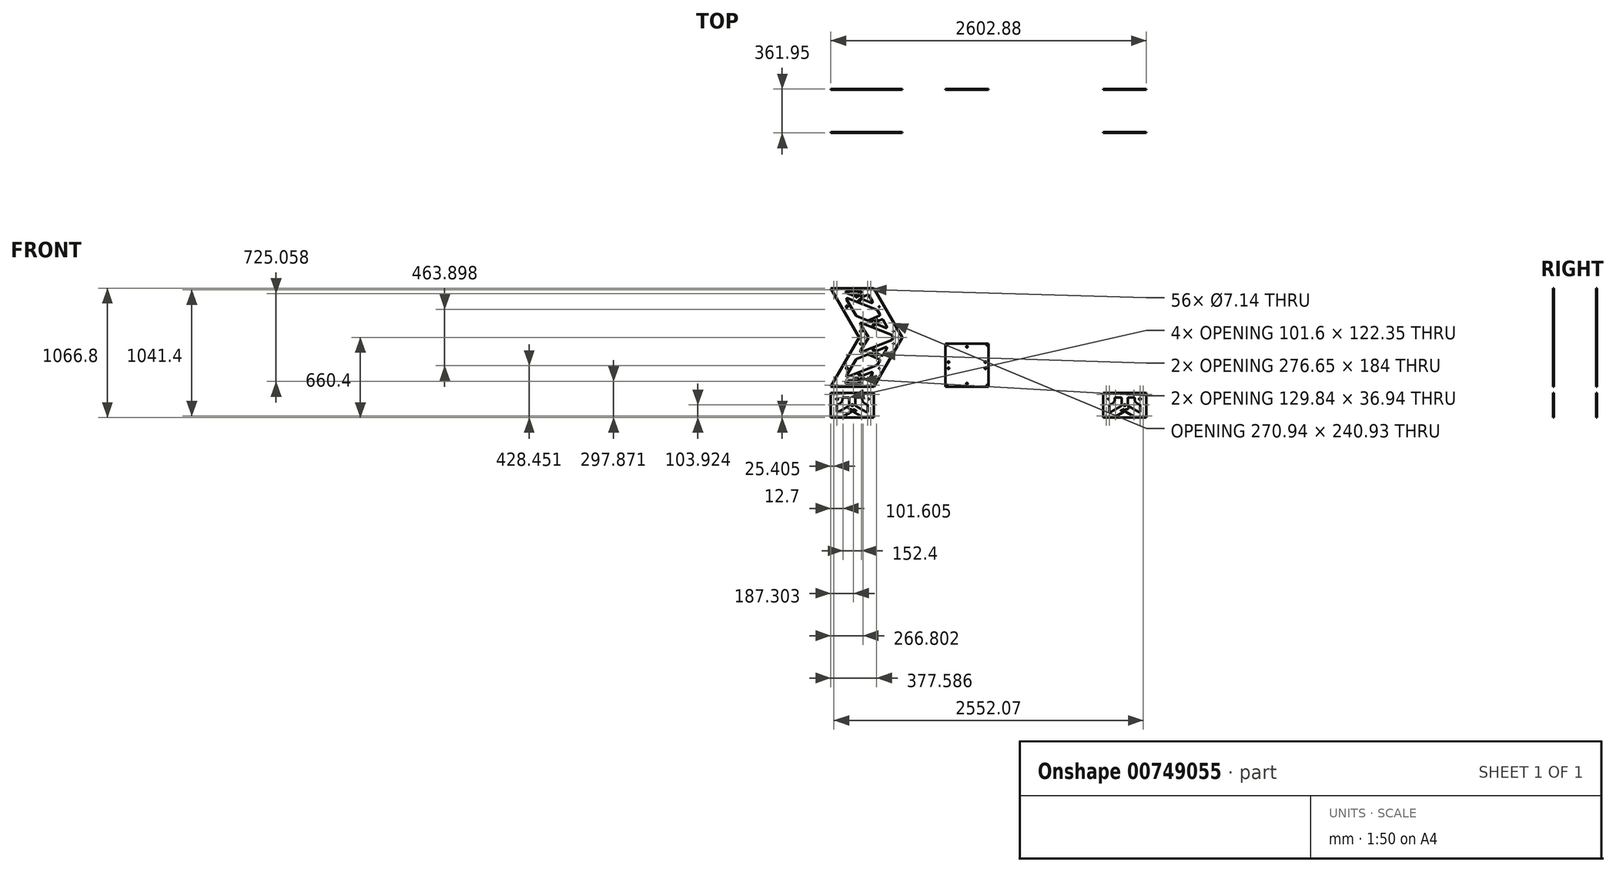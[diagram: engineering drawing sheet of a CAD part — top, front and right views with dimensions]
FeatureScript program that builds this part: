
annotation { "Feature Type Name" : "Feature", "Feature Type Description" : "" }
export const myFeature = defineFeature(function(context is Context, id is Id, definition is map)
    precondition{}
    {
        {
            var Q0;
            Q0=qCreatedBy(makeId("Front.planeOp"),FACE);
            var sketch = newSketch(context, id + "F0", { "sketchPlane" : qUnion([Q0])});
            skLineSegment(sketch, "E0.bottom", {"start": v(0, 0) * mm, "end": v(355.6, 0) * mm});
            skLineSegment(sketch, "E0.top", {"start": v(0, 355.6) * mm, "end": v(355.6, 355.6) * mm});
            skLineSegment(sketch, "E0.left", {"start": v(0, 0) * mm, "end": v(0, 355.6) * mm});
            skLineSegment(sketch, "E0.right", {"start": v(355.6, 0) * mm, "end": v(355.6, 355.6) * mm});
            skLineSegment(sketch, "E1", {"start": v(177.8, 355.6) * mm, "end": v(177.8, 0) * mm, "construction": true});
            skLineSegment(sketch, "E2", {"start": v(355.6, 177.8) * mm, "end": v(0, 177.8) * mm, "construction": true});
            skPoint(sketch, "E3", {"position": v(12.7, 342.9) * mm});
            skPoint(sketch, "E4.MirrorP", {"position": v(342.9, 342.9) * mm});
            skPoint(sketch, "E5.MirrorP", {"position": v(342.9, 12.7) * mm});
            skPoint(sketch, "E6.MirrorP", {"position": v(12.7, 12.7) * mm});
            skSolve(sketch);
        }
        {
            var Q0;
            Q0 = qSketchRegion(id + "F0", true);
            extrude(context, id + "F1", {"entities" : qUnion([Q0]), "depth" : 6.35 * mm, "offsetDistance" : 25.4 * mm});
        }
        {
            var Q0;
            Q0=sQuery(id+"F0.wireOp",VERTEX,"E3");
            var Q1;
            Q1=sQuery(id+"F0.wireOp",VERTEX,"E4.MirrorP");
            var Q2;
            Q2=sQuery(id+"F0.wireOp",VERTEX,"E5.MirrorP");
            var Q3;
            Q3=sQuery(id+"F0.wireOp",VERTEX,"E6.MirrorP");
            var Q4;
            Q4=makeQuery(id+"F1.opExtrude","SWEPT_BODY",BODY,{"disambiguationData":[OSD([sQuery(id+"F0.wireOp",EDGE,"E0.bottom"),sQuery(id+"F0.wireOp",EDGE,"E0.top"),sQuery(id+"F0.wireOp",EDGE,"E0.left"),sQuery(id+"F0.wireOp",EDGE,"E0.right")])]});
            hole(context, id + "F2", {"style" : HoleStyle.SIMPLE, "endStyle" : HoleEndStyle.BLIND, "oppositeDirection" : true, "standardTappedOrClearance" : lookupTablePath({ "standard" : "ANSI", "fit" : "Normal (ASME)", "size" : "1/4", "type" : "Clearance" }), "standardBlindInLast" : lookupTablePath({ "fit" : "Free", "standard" : "ANSI", "size" : "1/4", "type" : "Clearance" }), "holeDiameter" : 6.76 * mm, "majorDiameter" : 6.35 * mm, "holeDepth" : 26.06 * mm, "isTappedThrough" : true, "tappedDepth" : 22.25 * mm, "tapClearance" : 3, "locations" : qUnion([Q0, Q1, Q2, Q3]), "scope" : qUnion([Q4])});
        }
        {
            var Q0;
            Q0=makeQuery(id+"F1.opExtrude","CAP_FACE",FACE,{"disambiguationData":[OSD([sQuery(id+"F0.wireOp",EDGE,"E0.bottom"),sQuery(id+"F0.wireOp",EDGE,"E0.top"),sQuery(id+"F0.wireOp",EDGE,"E0.left"),sQuery(id+"F0.wireOp",EDGE,"E0.right")])],"isStart":false});
            var sketch = newSketch(context, id + "F3", { "sketchPlane" : qUnion([Q0])});
            skLineSegment(sketch, "E7", {"start": v(177.8, 355.6) * mm, "end": v(177.8, 0) * mm, "construction": true});
            skLineSegment(sketch, "E8", {"start": v(0, 177.8) * mm, "end": v(355.6, 177.8) * mm, "construction": true});
            skCircle(sketch, "E9", {"center": v(25.4, 203.2) * mm, "radius": 6.35 * mm});
            skCircle(sketch, "E10", {"center": v(177.8, 330.2) * mm, "radius": 6.35 * mm});
            skCircle(sketch, "E11.MirrorC", {"center": v(330.2, 203.2) * mm, "radius": 6.35 * mm});
            skCircle(sketch, "E12.MirrorC", {"center": v(25.4, 152.4) * mm, "radius": 6.35 * mm});
            skCircle(sketch, "E13.MirrorC", {"center": v(330.2, 152.4) * mm, "radius": 6.35 * mm});
            skCircle(sketch, "E14.MirrorC", {"center": v(177.8, 25.4) * mm, "radius": 6.35 * mm});
            skSolve(sketch);
        }
        {
            var Q0;
            Q0 = qSketchRegion(id + "F3", true);
            extrude(context, id + "F4", {"entities" : qUnion([Q0]), "operationType" : NewBodyOperationType.REMOVE, "oppositeDirection" : true, "depth" : 25.4 * mm, "offsetDistance" : 25.4 * mm});
        }
        {
            var Q0;
            Q0=qCreatedBy(makeId("Front.planeOp"),FACE);
            var sketch = newSketch(context, id + "F5", { "sketchPlane" : qUnion([Q0])});
            skLineSegment(sketch, "E15", {"start": v(-590.24, 0) * mm, "end": v(-945.84, 0) * mm});
            skLineSegment(sketch, "E16", {"start": v(-945.84, 0) * mm, "end": v(-711.2, 406.4) * mm});
            skLineSegment(sketch, "E17", {"start": v(-711.2, 406.4) * mm, "end": v(-945.84, 812.8) * mm});
            skLineSegment(sketch, "E18", {"start": v(-945.84, 812.8) * mm, "end": v(-590.24, 812.8) * mm});
            skLineSegment(sketch, "E19", {"start": v(-590.24, 812.8) * mm, "end": v(-355.6, 406.4) * mm});
            skLineSegment(sketch, "E20", {"start": v(-355.6, 406.4) * mm, "end": v(-590.24, 0) * mm});
            skSolve(sketch);
        }
        {
            var Q0;
            Q0 = qSketchRegion(id + "F5", true);
            extrude(context, id + "F6", {"entities" : qUnion([Q0]), "depth" : 6.35 * mm, "offsetDistance" : 25.4 * mm});
        }
        {
            var Q0;
            Q0=makeQuery(id+"F6.opExtrude","CAP_FACE",FACE,{"disambiguationData":[OSD([sQuery(id+"F5.wireOp",EDGE,"E15"),sQuery(id+"F5.wireOp",EDGE,"E16"),sQuery(id+"F5.wireOp",EDGE,"E17"),sQuery(id+"F5.wireOp",EDGE,"E18"),sQuery(id+"F5.wireOp",EDGE,"E19"),sQuery(id+"F5.wireOp",EDGE,"E20")])],"isStart":false});
            var sketch = newSketch(context, id + "F7", { "sketchPlane" : qUnion([Q0])});
            skLineSegment(sketch, "E21", {"start": v(-768.04, 0) * mm, "end": v(-768.04, 812.8) * mm, "construction": true});
            skPoint(sketch, "E22", {"position": v(-895.04, 12.7) * mm});
            skLineSegment(sketch, "E23", {"start": v(-355.6, 406.4) * mm, "end": v(-711.2, 406.4) * mm, "construction": true});
            skPoint(sketch, "E24.MirrorP", {"position": v(-641.04, 12.7) * mm});
            skPoint(sketch, "E25.MirrorP", {"position": v(-895.04, 800.1) * mm});
            skPoint(sketch, "E26.MirrorP", {"position": v(-641.04, 800.1) * mm});
            skPoint(sketch, "E27.startSnap0", {"position": v(-533.4, 406.4) * mm});
            skPoint(sketch, "E28", {"position": v(-413.73, 406.4) * mm});
            skPoint(sketch, "E29.MirrorP", {"position": v(-667.73, 406.4) * mm});
            skLineSegment(sketch, "E30", {"start": v(-582.9, 12.7) * mm, "end": v(-938.5, 12.7) * mm, "construction": true});
            skPoint(sketch, "E31", {"position": v(-920.44, 12.7) * mm});
            skPoint(sketch, "E32", {"position": v(-615.64, 12.7) * mm});
            skPoint(sketch, "E33.MirrorP", {"position": v(-615.64, 800.1) * mm});
            skPoint(sketch, "E34.MirrorP", {"position": v(-920.44, 800.1) * mm});
            skPoint(sketch, "E35", {"position": v(-693.13, 406.4) * mm});
            skPoint(sketch, "E36", {"position": v(-388.33, 406.4) * mm});
            skLineSegment(sketch, "E37", {"start": v(-895.04, 12.7) * mm, "end": v(-667.73, 406.4) * mm, "construction": true});
            skLineSegment(sketch, "E38", {"start": v(-641.04, 12.7) * mm, "end": v(-413.73, 406.4) * mm, "construction": true});
            skSolve(sketch);
        }
        {
            var Q0;
            Q0=sQuery(id+"F7.wireOp",VERTEX,"E25.MirrorP");
            var Q1;
            Q1=sQuery(id+"F7.wireOp",VERTEX,"E26.MirrorP");
            var Q2;
            Q2=sQuery(id+"F7.wireOp",VERTEX,"E29.MirrorP");
            var Q3;
            Q3=sQuery(id+"F7.wireOp",VERTEX,"E28");
            var Q4;
            Q4=sQuery(id+"F7.wireOp",VERTEX,"E24.MirrorP");
            var Q5;
            Q5=sQuery(id+"F7.wireOp",VERTEX,"E22");
            var Q6;
            Q6=sQuery(id+"F7.wireOp",VERTEX,"E31");
            var Q7;
            Q7=sQuery(id+"F7.wireOp",VERTEX,"E32");
            var Q8;
            Q8=sQuery(id+"F7.wireOp",VERTEX,"E33.MirrorP");
            var Q9;
            Q9=sQuery(id+"F7.wireOp",VERTEX,"E34.MirrorP");
            var Q10;
            Q10=sQuery(id+"F7.wireOp",VERTEX,"E35");
            var Q11;
            Q11=sQuery(id+"F7.wireOp",VERTEX,"E36");
            var Q12;
            Q12=makeQuery(id+"F6.opExtrude","SWEPT_BODY",BODY,{"disambiguationData":[OSD([sQuery(id+"F5.wireOp",EDGE,"E15"),sQuery(id+"F5.wireOp",EDGE,"E16"),sQuery(id+"F5.wireOp",EDGE,"E17"),sQuery(id+"F5.wireOp",EDGE,"E18"),sQuery(id+"F5.wireOp",EDGE,"E19"),sQuery(id+"F5.wireOp",EDGE,"E20")])]});
            hole(context, id + "F8", {"style" : HoleStyle.SIMPLE, "endStyle" : HoleEndStyle.BLIND, "standardTappedOrClearance" : lookupTablePath({ "fit" : "Normal (ASME)", "standard" : "ANSI", "size" : "1/4", "type" : "Clearance" }), "standardBlindInLast" : lookupTablePath({ "fit" : "Normal", "standard" : "ANSI", "size" : "1/4", "type" : "Clearance" }), "holeDiameter" : 7.14 * mm, "majorDiameter" : 6.35 * mm, "holeDepth" : 26.06 * mm, "isTappedThrough" : true, "tappedDepth" : 22.25 * mm, "tapClearance" : 3, "locations" : qUnion([Q0, Q1, Q2, Q3, Q4, Q5, Q6, Q7, Q8, Q9, Q10, Q11]), "scope" : qUnion([Q12])});
        }
        {
            var Q0;
            Q0=makeQuery(id+"F6.opExtrude","CAP_FACE",FACE,{"disambiguationData":[OSD([sQuery(id+"F5.wireOp",EDGE,"E15"),sQuery(id+"F5.wireOp",EDGE,"E16"),sQuery(id+"F5.wireOp",EDGE,"E17"),sQuery(id+"F5.wireOp",EDGE,"E18"),sQuery(id+"F5.wireOp",EDGE,"E19"),sQuery(id+"F5.wireOp",EDGE,"E20")])],"isStart":false});
            var sketch = newSketch(context, id + "F9", { "sketchPlane" : qUnion([Q0])});
            skLineSegment(sketch, "E39", {"start": v(-768.04, 0) * mm, "end": v(-533.4, 406.4) * mm, "construction": true});
            skLineSegment(sketch, "E40", {"start": v(-533.4, 406.4) * mm, "end": v(-768.04, 812.8) * mm, "construction": true});
            skPoint(sketch, "E41", {"position": v(-592.06, 304.8) * mm});
            skLineSegment(sketch, "E42", {"start": v(-711.2, 406.4) * mm, "end": v(-355.6, 406.4) * mm, "construction": true});
            skPoint(sketch, "E43.MirrorP", {"position": v(-592.06, 508) * mm});
            skLineSegment(sketch, "E44", {"start": v(-634.69, 0) * mm, "end": v(-400.05, 406.4) * mm, "construction": true});
            skLineSegment(sketch, "E45", {"start": v(-400.05, 406.4) * mm, "end": v(-634.69, 812.8) * mm, "construction": true});
            skPoint(sketch, "E46", {"position": v(-546.7, 152.4) * mm});
            skPoint(sketch, "E47", {"position": v(-429.38, 355.6) * mm});
            skPoint(sketch, "E48.MirrorP", {"position": v(-429.38, 457.2) * mm});
            skPoint(sketch, "E49.MirrorP", {"position": v(-546.7, 660.4) * mm});
            skLineSegment(sketch, "E50", {"start": v(-901.39, 0) * mm, "end": v(-666.75, 406.4) * mm, "construction": true});
            skLineSegment(sketch, "E51", {"start": v(-666.75, 406.4) * mm, "end": v(-901.39, 812.8) * mm, "construction": true});
            skPoint(sketch, "E52", {"position": v(-813.4, 152.4) * mm});
            skPoint(sketch, "E53", {"position": v(-696.08, 355.6) * mm});
            skPoint(sketch, "E54.MirrorP", {"position": v(-696.08, 457.2) * mm});
            skPoint(sketch, "E55.MirrorP", {"position": v(-813.4, 660.4) * mm});
            skLineSegment(sketch, "E56", {"start": v(-429.38, 355.6) * mm, "end": v(-696.08, 355.6) * mm, "construction": true});
            skLineSegment(sketch, "E57", {"start": v(-458.7, 304.8) * mm, "end": v(-725.4, 304.8) * mm, "construction": true});
            skPoint(sketch, "E58", {"position": v(-563.18, 261.14) * mm});
            skPoint(sketch, "E59", {"position": v(-579.9, 268.3) * mm});
            skPoint(sketch, "E60", {"position": v(-599.78, 267.16) * mm});
            skPoint(sketch, "E61", {"position": v(-617.61, 276.07) * mm});
            skPoint(sketch, "E62", {"position": v(-709.38, 101.6) * mm});
            skPoint(sketch, "E63", {"position": v(-680.5, 57.94) * mm});
            skPoint(sketch, "E64", {"position": v(-697.2, 65.1) * mm});
            skPoint(sketch, "E65", {"position": v(-717.1, 63.96) * mm});
            skPoint(sketch, "E66", {"position": v(-734.93, 72.87) * mm});
            skPoint(sketch, "E67.MirrorP", {"position": v(-563.18, 551.66) * mm});
            skPoint(sketch, "E68.MirrorP", {"position": v(-579.9, 544.5) * mm});
            skPoint(sketch, "E69.MirrorP", {"position": v(-599.78, 545.64) * mm});
            skPoint(sketch, "E70.MirrorP", {"position": v(-617.61, 536.73) * mm});
            skPoint(sketch, "E71.MirrorP", {"position": v(-680.5, 754.86) * mm});
            skPoint(sketch, "E72.MirrorP", {"position": v(-697.2, 747.7) * mm});
            skPoint(sketch, "E73.MirrorP", {"position": v(-717.1, 748.84) * mm});
            skPoint(sketch, "E74.MirrorP", {"position": v(-734.93, 739.93) * mm});
            skPoint(sketch, "E75.MirrorP", {"position": v(-709.38, 711.2) * mm});
            skSolve(sketch);
        }
        {
            var Q0;
            Q0=sQuery(id+"F9.wireOp",VERTEX,"8cdeff21-2003-4bda-b2ca-6eb4603f8591");
            var Q1;
            Q1=sQuery(id+"F9.wireOp",VERTEX,"E41");
            var Q2;
            Q2=sQuery(id+"F9.wireOp",VERTEX,"E43.MirrorP");
            var Q3;
            Q3=sQuery(id+"F9.wireOp",VERTEX,"d93e7216-f609-4520-8570-f6b935fa21990.MirrorP");
            var Q4;
            Q4=sQuery(id+"F9.wireOp",VERTEX,"E46");
            var Q5;
            Q5=sQuery(id+"F9.wireOp",VERTEX,"E47");
            var Q6;
            Q6=sQuery(id+"F9.wireOp",VERTEX,"E48.MirrorP");
            var Q7;
            Q7=sQuery(id+"F9.wireOp",VERTEX,"E49.MirrorP");
            var Q8;
            Q8=sQuery(id+"F9.wireOp",VERTEX,"E52");
            var Q9;
            Q9=sQuery(id+"F9.wireOp",VERTEX,"E53");
            var Q10;
            Q10=sQuery(id+"F9.wireOp",VERTEX,"E54.MirrorP");
            var Q11;
            Q11=sQuery(id+"F9.wireOp",VERTEX,"E55.MirrorP");
            var Q12;
            Q12=sQuery(id+"F9.wireOp",VERTEX,"E70.MirrorP");
            var Q13;
            Q13=sQuery(id+"F9.wireOp",VERTEX,"E69.MirrorP");
            var Q14;
            Q14=sQuery(id+"F9.wireOp",VERTEX,"E68.MirrorP");
            var Q15;
            Q15=sQuery(id+"F9.wireOp",VERTEX,"E67.MirrorP");
            var Q16;
            Q16=sQuery(id+"F9.wireOp",VERTEX,"E74.MirrorP");
            var Q17;
            Q17=sQuery(id+"F9.wireOp",VERTEX,"E73.MirrorP");
            var Q18;
            Q18=sQuery(id+"F9.wireOp",VERTEX,"E72.MirrorP");
            var Q19;
            Q19=sQuery(id+"F9.wireOp",VERTEX,"E71.MirrorP");
            var Q20;
            Q20=sQuery(id+"F9.wireOp",VERTEX,"E75.MirrorP");
            var Q21;
            Q21=sQuery(id+"F9.wireOp",VERTEX,"E61");
            var Q22;
            Q22=sQuery(id+"F9.wireOp",VERTEX,"E60");
            var Q23;
            Q23=sQuery(id+"F9.wireOp",VERTEX,"E59");
            var Q24;
            Q24=sQuery(id+"F9.wireOp",VERTEX,"E58");
            var Q25;
            Q25=sQuery(id+"F9.wireOp",VERTEX,"E62");
            var Q26;
            Q26=sQuery(id+"F9.wireOp",VERTEX,"E66");
            var Q27;
            Q27=sQuery(id+"F9.wireOp",VERTEX,"E65");
            var Q28;
            Q28=sQuery(id+"F9.wireOp",VERTEX,"E64");
            var Q29;
            Q29=sQuery(id+"F9.wireOp",VERTEX,"E63");
            var Q30;
            Q30=makeQuery(id+"F6.opExtrude","SWEPT_BODY",BODY,{"disambiguationData":[OSD([sQuery(id+"F5.wireOp",EDGE,"E15"),sQuery(id+"F5.wireOp",EDGE,"E16"),sQuery(id+"F5.wireOp",EDGE,"E17"),sQuery(id+"F5.wireOp",EDGE,"E18"),sQuery(id+"F5.wireOp",EDGE,"E19"),sQuery(id+"F5.wireOp",EDGE,"E20")])]});
            hole(context, id + "F10", {"style" : HoleStyle.SIMPLE, "endStyle" : HoleEndStyle.BLIND, "holeDiameter" : 6.35 * mm, "majorDiameter" : 6.35 * mm, "holeDepth" : 26.06 * mm, "isTappedThrough" : true, "tappedDepth" : 22.25 * mm, "tapClearance" : 3, "locations" : qUnion([Q0, Q1, Q2, Q3, Q4, Q5, Q6, Q7, Q8, Q9, Q10, Q11, Q12, Q13, Q14, Q15, Q16, Q17, Q18, Q19, Q20, Q21, Q22, Q23, Q24, Q25, Q26, Q27, Q28, Q29]), "scope" : qUnion([Q30])});
        }
        {
            var Q0;
            Q0=makeQuery(id+"F6.opExtrude","SWEPT_BODY",BODY,{"disambiguationData":[OSD([sQuery(id+"F5.wireOp",EDGE,"E15"),sQuery(id+"F5.wireOp",EDGE,"E16"),sQuery(id+"F5.wireOp",EDGE,"E17"),sQuery(id+"F5.wireOp",EDGE,"E18"),sQuery(id+"F5.wireOp",EDGE,"E19"),sQuery(id+"F5.wireOp",EDGE,"E20")])]});
            var Q1;
            Q1=makeQuery(id+"F6.opExtrude","CAP_FACE",FACE,{"disambiguationData":[OSD([sQuery(id+"F5.wireOp",EDGE,"E15"),sQuery(id+"F5.wireOp",EDGE,"E16"),sQuery(id+"F5.wireOp",EDGE,"E17"),sQuery(id+"F5.wireOp",EDGE,"E18"),sQuery(id+"F5.wireOp",EDGE,"E19"),sQuery(id+"F5.wireOp",EDGE,"E20")])],"isStart":false});
            transform(context, id + "F11", {"entities" : qUnion([Q0]), "transformType" : TransformType.TRANSLATION_DISTANCE, "transformDirection" : qUnion([Q1]), "distance" : 355.6 * mm, "makeCopy" : true});
        }
        {
            var Q0;
            Q0=makeQuery(id+"F11.opPattern","COPY",FACE,{"derivedFrom":makeQuery(id+"F6.opExtrude","CAP_FACE",FACE,{"disambiguationData":[OSD([sQuery(id+"F5.wireOp",EDGE,"E15"),sQuery(id+"F5.wireOp",EDGE,"E16"),sQuery(id+"F5.wireOp",EDGE,"E17"),sQuery(id+"F5.wireOp",EDGE,"E18"),sQuery(id+"F5.wireOp",EDGE,"E19"),sQuery(id+"F5.wireOp",EDGE,"E20")])],"isStart":false}),"instanceName":"1"});
            var sketch = newSketch(context, id + "F12", { "sketchPlane" : qUnion([Q0])});
            skLineSegment(sketch, "E76", {"start": v(-711.2, 406.4) * mm, "end": v(-355.6, 406.4) * mm, "construction": true});
            skLineSegment(sketch, "E77", {"start": v(-633.28, 755.38) * mm, "end": v(-602.21, 701.56) * mm});
            skLineSegment(sketch, "E78", {"start": v(-819.52, 775.14) * mm, "end": v(-758.08, 750.9) * mm});
            skLineSegment(sketch, "E79", {"start": v(-808.71, 729.92) * mm, "end": v(-564.55, 633.57) * mm});
            skLineSegment(sketch, "E80", {"start": v(-735.6, 583.39) * mm, "end": v(-642.86, 546.8) * mm});
            skLineSegment(sketch, "E81", {"start": v(-695.06, 526.43) * mm, "end": v(-445.93, 428.12) * mm});
            skLineSegment(sketch, "E82.trimOffspring", {"start": v(-702.8, 517.21) * mm, "end": v(-637.03, 409.71) * mm});
            skLineSegment(sketch, "E83.trimOffspring", {"start": v(-442.77, 425.4) * mm, "end": v(-433.63, 409.58) * mm});
            skLineSegment(sketch, "E84.trimOffspring", {"start": v(-561.38, 630.84) * mm, "end": v(-541.53, 596.46) * mm});
            skLineSegment(sketch, "E85.trimOffspring", {"start": v(-816.54, 720.84) * mm, "end": v(-738.76, 586.12) * mm});
            skLineSegment(sketch, "E86.MirrorCS", {"start": v(-702.8, 295.59) * mm, "end": v(-637.03, 403.09) * mm});
            skLineSegment(sketch, "E87.MirrorCS", {"start": v(-695.06, 286.37) * mm, "end": v(-445.93, 384.68) * mm});
            skLineSegment(sketch, "E88.MirrorCS", {"start": v(-735.6, 229.41) * mm, "end": v(-642.86, 266) * mm});
            skLineSegment(sketch, "E89.MirrorCS", {"start": v(-561.38, 181.96) * mm, "end": v(-541.53, 216.34) * mm});
            skLineSegment(sketch, "E90.MirrorCS", {"start": v(-442.77, 387.4) * mm, "end": v(-433.63, 403.23) * mm});
            skLineSegment(sketch, "E91.MirrorCS", {"start": v(-816.54, 91.96) * mm, "end": v(-738.76, 226.68) * mm});
            skLineSegment(sketch, "E92.MirrorCS", {"start": v(-808.71, 82.88) * mm, "end": v(-564.55, 179.23) * mm});
            skLineSegment(sketch, "E93.MirrorCS", {"start": v(-819.52, 37.66) * mm, "end": v(-758.08, 61.9) * mm});
            skLineSegment(sketch, "E94", {"start": v(-817.19, 787.4) * mm, "end": v(-699.9, 787.4) * mm});
            skPoint(sketch, "E95.start.orphan", {"position": v(-869.64, 812.8) * mm});
            skPoint(sketch, "E96.orphan", {"position": v(-666.44, 812.8) * mm});
            skLineSegment(sketch, "E97.MirrorCS", {"start": v(-817.19, 25.4) * mm, "end": v(-699.9, 25.4) * mm});
            skPoint(sketch, "E98.orphan", {"position": v(-666.44, 0) * mm});
            skLineSegment(sketch, "E99", {"start": v(-635, 406.4) * mm, "end": v(-869.64, 0) * mm, "construction": true});
            skPoint(sketch, "E100.visualSharp", {"position": v(-850.58, 787.4) * mm});
            skArc(sketch, "E100.filletArc", {"start": v(-817.19, 787.4) * mm, "mid": v(-823.43, 782.24) * mm, "end": v(-819.52, 775.14) * mm});
            skPoint(sketch, "E101.visualSharp", {"position": v(-593.11, 685.8) * mm});
            skArc(sketch, "E101.filletArc", {"start": v(-610.04, 692.48) * mm, "mid": v(-602.9, 694.24) * mm, "end": v(-602.21, 701.56) * mm});
            skPoint(sketch, "E102.visualSharp", {"position": v(-651.77, 787.4) * mm});
            skPoint(sketch, "E103.visualSharp", {"position": v(-562.49, 632.76) * mm});
            skArc(sketch, "E103.filletArc", {"start": v(-561.38, 630.84) * mm, "mid": v(-562.73, 632.47) * mm, "end": v(-564.55, 633.57) * mm});
            skPoint(sketch, "E104.visualSharp", {"position": v(-474.5, 480.36) * mm});
            skArc(sketch, "E104.filletArc", {"start": v(-491.43, 487.04) * mm, "mid": v(-484.29, 488.8) * mm, "end": v(-483.6, 496.12) * mm});
            skPoint(sketch, "E105.visualSharp", {"position": v(-737.65, 584.2) * mm});
            skArc(sketch, "E105.filletArc", {"start": v(-738.76, 586.12) * mm, "mid": v(-737.4, 584.48) * mm, "end": v(-735.6, 583.39) * mm});
            skPoint(sketch, "E106.visualSharp", {"position": v(-825.64, 736.6) * mm});
            skArc(sketch, "E106.filletArc", {"start": v(-808.71, 729.92) * mm, "mid": v(-815.85, 728.16) * mm, "end": v(-816.54, 720.84) * mm});
            skPoint(sketch, "E107.visualSharp", {"position": v(-431.8, 406.4) * mm});
            skArc(sketch, "E107.filletArc", {"start": v(-433.63, 403.23) * mm, "mid": v(-432.78, 406.4) * mm, "end": v(-433.63, 409.58) * mm});
            skPoint(sketch, "E108.visualSharp", {"position": v(-443.87, 385.49) * mm});
            skArc(sketch, "E108.filletArc", {"start": v(-445.93, 384.68) * mm, "mid": v(-444.12, 385.77) * mm, "end": v(-442.77, 387.4) * mm});
            skPoint(sketch, "E109.visualSharp", {"position": v(-712.71, 279.4) * mm});
            skArc(sketch, "E109.filletArc", {"start": v(-702.8, 295.59) * mm, "mid": v(-702.26, 288.19) * mm, "end": v(-695.06, 286.37) * mm});
            skPoint(sketch, "E110.visualSharp", {"position": v(-712.71, 533.4) * mm});
            skArc(sketch, "E110.filletArc", {"start": v(-695.06, 526.43) * mm, "mid": v(-702.26, 524.61) * mm, "end": v(-702.8, 517.21) * mm});
            skPoint(sketch, "E111.visualSharp", {"position": v(-635, 406.4) * mm});
            skArc(sketch, "E111.filletArc", {"start": v(-637.03, 403.09) * mm, "mid": v(-636.1, 406.4) * mm, "end": v(-637.03, 409.71) * mm});
            skPoint(sketch, "E112.visualSharp", {"position": v(-593.11, 127) * mm});
            skPoint(sketch, "E113.visualSharp", {"position": v(-651.77, 25.4) * mm});
            skPoint(sketch, "E114.visualSharp", {"position": v(-443.87, 427.31) * mm});
            skArc(sketch, "E114.filletArc", {"start": v(-442.77, 425.4) * mm, "mid": v(-444.12, 427.03) * mm, "end": v(-445.93, 428.12) * mm});
            skPoint(sketch, "E115.visualSharp", {"position": v(-850.58, 25.4) * mm});
            skArc(sketch, "E115.filletArc", {"start": v(-819.52, 37.66) * mm, "mid": v(-823.43, 30.56) * mm, "end": v(-817.19, 25.4) * mm});
            skPoint(sketch, "E116.visualSharp", {"position": v(-825.64, 76.2) * mm});
            skArc(sketch, "E116.filletArc", {"start": v(-816.54, 91.96) * mm, "mid": v(-815.85, 84.64) * mm, "end": v(-808.71, 82.88) * mm});
            skPoint(sketch, "E117.visualSharp", {"position": v(-562.49, 180.04) * mm});
            skArc(sketch, "E117.filletArc", {"start": v(-564.55, 179.23) * mm, "mid": v(-562.73, 180.33) * mm, "end": v(-561.38, 181.96) * mm});
            skPoint(sketch, "E118.visualSharp", {"position": v(-474.5, 332.44) * mm});
            skArc(sketch, "E118.filletArc", {"start": v(-483.6, 316.68) * mm, "mid": v(-484.29, 324) * mm, "end": v(-491.43, 325.76) * mm});
            skPoint(sketch, "E119.visualSharp", {"position": v(-737.65, 228.6) * mm});
            skArc(sketch, "E119.filletArc", {"start": v(-735.6, 229.41) * mm, "mid": v(-737.4, 228.32) * mm, "end": v(-738.76, 226.68) * mm});
            skLineSegment(sketch, "E120", {"start": v(-638, 265.93) * mm, "end": v(-544.5, 225.34) * mm});
            skLineSegment(sketch, "E121", {"start": v(-576.23, 280.65) * mm, "end": v(-524, 257.97) * mm});
            skLineSegment(sketch, "E122", {"start": v(-528.38, 239.11) * mm, "end": v(-615.35, 276.86) * mm, "construction": true});
            skLineSegment(sketch, "E123", {"start": v(-753.22, 61.82) * mm, "end": v(-697.38, 37.57) * mm});
            skLineSegment(sketch, "E124", {"start": v(-691.45, 76.54) * mm, "end": v(-641.31, 54.77) * mm});
            skLineSegment(sketch, "E125", {"start": v(-730.58, 72.75) * mm, "end": v(-630.77, 29.43) * mm, "construction": true});
            skLineSegment(sketch, "E126.trimOffspring", {"start": v(-691.26, 88.27) * mm, "end": v(-610.04, 120.32) * mm});
            skLineSegment(sketch, "E127.trimOffspring", {"start": v(-633.28, 57.42) * mm, "end": v(-602.21, 111.24) * mm});
            skLineSegment(sketch, "E128.trimOffspring", {"start": v(-515.97, 260.62) * mm, "end": v(-483.6, 316.68) * mm});
            skLineSegment(sketch, "E129.trimOffspring", {"start": v(-576.03, 292.38) * mm, "end": v(-491.43, 325.76) * mm});
            skPoint(sketch, "E130.visualSharp", {"position": v(-636.11, 52.52) * mm});
            skArc(sketch, "E130.filletArc", {"start": v(-641.31, 54.77) * mm, "mid": v(-636.8, 54.57) * mm, "end": v(-633.28, 57.42) * mm});
            skPoint(sketch, "E131.visualSharp", {"position": v(-669.33, 25.4) * mm});
            skArc(sketch, "E131.filletArc", {"start": v(-699.9, 25.4) * mm, "mid": v(-693.69, 30.46) * mm, "end": v(-697.38, 37.57) * mm});
            skPoint(sketch, "E132.visualSharp", {"position": v(-537.97, 222.5) * mm});
            skArc(sketch, "E132.filletArc", {"start": v(-541.53, 216.34) * mm, "mid": v(-541, 221.5) * mm, "end": v(-544.5, 225.34) * mm});
            skPoint(sketch, "E133.visualSharp", {"position": v(-518.8, 255.72) * mm});
            skArc(sketch, "E133.filletArc", {"start": v(-524, 257.97) * mm, "mid": v(-519.47, 257.77) * mm, "end": v(-515.97, 260.62) * mm});
            skPoint(sketch, "E134.visualSharp", {"position": v(-590.3, 286.75) * mm});
            skArc(sketch, "E134.filletArc", {"start": v(-576.03, 292.38) * mm, "mid": v(-580.05, 286.58) * mm, "end": v(-576.23, 280.65) * mm});
            skPoint(sketch, "E135.visualSharp", {"position": v(-640.41, 266.97) * mm});
            skArc(sketch, "E135.filletArc", {"start": v(-638, 265.93) * mm, "mid": v(-640.42, 266.45) * mm, "end": v(-642.86, 266) * mm});
            skPoint(sketch, "E136.visualSharp", {"position": v(-755.64, 62.87) * mm});
            skArc(sketch, "E136.filletArc", {"start": v(-753.22, 61.82) * mm, "mid": v(-755.65, 62.34) * mm, "end": v(-758.08, 61.9) * mm});
            skPoint(sketch, "E137.visualSharp", {"position": v(-705.52, 82.64) * mm});
            skArc(sketch, "E137.filletArc", {"start": v(-691.26, 88.27) * mm, "mid": v(-695.28, 82.47) * mm, "end": v(-691.45, 76.54) * mm});
            skLineSegment(sketch, "E138.MirrorCS", {"start": v(-576.23, 532.15) * mm, "end": v(-524, 554.83) * mm});
            skArc(sketch, "E139.MirrorCS", {"start": v(-576.03, 520.42) * mm, "mid": v(-580.05, 526.22) * mm, "end": v(-576.23, 532.15) * mm});
            skArc(sketch, "E140.MirrorCS", {"start": v(-524, 554.83) * mm, "mid": v(-519.47, 555.03) * mm, "end": v(-515.97, 552.18) * mm});
            skArc(sketch, "E141.MirrorCS", {"start": v(-638, 546.87) * mm, "mid": v(-640.42, 546.35) * mm, "end": v(-642.86, 546.8) * mm});
            skLineSegment(sketch, "E142.MirrorCS", {"start": v(-638, 546.87) * mm, "end": v(-544.5, 587.46) * mm});
            skArc(sketch, "E143.MirrorCS", {"start": v(-541.53, 596.46) * mm, "mid": v(-541, 591.3) * mm, "end": v(-544.5, 587.46) * mm});
            skLineSegment(sketch, "E144.MirrorCS", {"start": v(-691.45, 736.26) * mm, "end": v(-641.31, 758.03) * mm});
            skArc(sketch, "E145.MirrorCS", {"start": v(-641.31, 758.03) * mm, "mid": v(-636.8, 758.23) * mm, "end": v(-633.28, 755.38) * mm});
            skArc(sketch, "E146.MirrorCS", {"start": v(-691.26, 724.53) * mm, "mid": v(-695.28, 730.33) * mm, "end": v(-691.45, 736.26) * mm});
            skLineSegment(sketch, "E147.MirrorCS", {"start": v(-753.22, 750.98) * mm, "end": v(-697.38, 775.23) * mm});
            skArc(sketch, "E148.MirrorCS", {"start": v(-699.9, 787.4) * mm, "mid": v(-693.69, 782.34) * mm, "end": v(-697.38, 775.23) * mm});
            skArc(sketch, "E149.MirrorCS", {"start": v(-753.22, 750.98) * mm, "mid": v(-755.65, 750.46) * mm, "end": v(-758.08, 750.9) * mm});
            skLineSegment(sketch, "E150.trimOffspring", {"start": v(-691.26, 724.53) * mm, "end": v(-610.04, 692.48) * mm});
            skLineSegment(sketch, "E151.trimOffspring", {"start": v(-576.03, 520.42) * mm, "end": v(-491.43, 487.04) * mm});
            skLineSegment(sketch, "E152.trimOffspring", {"start": v(-515.97, 552.18) * mm, "end": v(-483.6, 496.12) * mm});
            skArc(sketch, "E153.filletArc", {"start": v(-602.21, 111.24) * mm, "mid": v(-602.9, 118.56) * mm, "end": v(-610.04, 120.32) * mm});
            skSolve(sketch);
        }
        {
            var Q0;
            Q0 = qSketchRegion(id + "F12", true);
            extrude(context, id + "F13", {"entities" : qUnion([Q0]), "operationType" : NewBodyOperationType.REMOVE, "oppositeDirection" : true, "depth" : 25.4 * mm, "offsetDistance" : 25.4 * mm});
        }
        {
            var Q0;
            Q0=sQuery(id+"F9.wireOp",VERTEX,"E62");
            var Q1;
            Q1=sQuery(id+"F9.wireOp",VERTEX,"E41");
            var Q2;
            Q2=sQuery(id+"F9.wireOp",VERTEX,"E43.MirrorP");
            var Q3;
            Q3=sQuery(id+"F9.wireOp",VERTEX,"E75.MirrorP");
            var Q4;
            Q4=sQuery(id+"F9.wireOp",VERTEX,"E52");
            var Q5;
            Q5=sQuery(id+"F9.wireOp",VERTEX,"E53");
            var Q6;
            Q6=sQuery(id+"F9.wireOp",VERTEX,"E54.MirrorP");
            var Q7;
            Q7=sQuery(id+"F9.wireOp",VERTEX,"E55.MirrorP");
            var Q8;
            Q8=makeQuery(id+"F6.opExtrude","SWEPT_BODY",BODY,{"disambiguationData":[OSD([sQuery(id+"F5.wireOp",EDGE,"E15"),sQuery(id+"F5.wireOp",EDGE,"E16"),sQuery(id+"F5.wireOp",EDGE,"E17"),sQuery(id+"F5.wireOp",EDGE,"E18"),sQuery(id+"F5.wireOp",EDGE,"E19"),sQuery(id+"F5.wireOp",EDGE,"E20")])]});
            hole(context, id + "F14", {"style" : HoleStyle.SIMPLE, "endStyle" : HoleEndStyle.BLIND, "holeDiameter" : 15.88 * mm, "majorDiameter" : 6.35 * mm, "holeDepth" : 6.35 * mm, "isTappedThrough" : true, "tappedDepth" : 22.25 * mm, "tapClearance" : 3, "locations" : qUnion([Q0, Q1, Q2, Q3, Q4, Q5, Q6, Q7]), "scope" : qUnion([Q8])});
        }
        {
            var Q0;
            Q0=makeQuery(id+"F11.opPattern","COPY",FACE,{"derivedFrom":makeQuery(id+"F6.opExtrude","CAP_FACE",FACE,{"disambiguationData":[OSD([sQuery(id+"F5.wireOp",EDGE,"E15"),sQuery(id+"F5.wireOp",EDGE,"E16"),sQuery(id+"F5.wireOp",EDGE,"E17"),sQuery(id+"F5.wireOp",EDGE,"E18"),sQuery(id+"F5.wireOp",EDGE,"E19"),sQuery(id+"F5.wireOp",EDGE,"E20")])],"isStart":false}),"instanceName":"1"});
            var sketch = newSketch(context, id + "F15", { "sketchPlane" : qUnion([Q0])});
            skPoint(sketch, "E154", {"position": v(-813.4, 152.4) * mm});
            skPoint(sketch, "E155", {"position": v(-709.38, 101.6) * mm});
            skPoint(sketch, "E156", {"position": v(-592.06, 304.8) * mm});
            skPoint(sketch, "E157", {"position": v(-696.08, 355.6) * mm});
            skPoint(sketch, "E158", {"position": v(-696.08, 457.2) * mm});
            skPoint(sketch, "E159", {"position": v(-592.06, 508) * mm});
            skPoint(sketch, "E160", {"position": v(-813.4, 660.4) * mm});
            skPoint(sketch, "E161", {"position": v(-709.38, 711.2) * mm});
            skSolve(sketch);
        }
        {
            var Q0;
            Q0=sQuery(id+"F15.wireOp",VERTEX,"E160");
            var Q1;
            Q1=sQuery(id+"F15.wireOp",VERTEX,"E161");
            var Q2;
            Q2=sQuery(id+"F15.wireOp",VERTEX,"E159");
            var Q3;
            Q3=sQuery(id+"F15.wireOp",VERTEX,"E158");
            var Q4;
            Q4=sQuery(id+"F15.wireOp",VERTEX,"E157");
            var Q5;
            Q5=sQuery(id+"F15.wireOp",VERTEX,"E156");
            var Q6;
            Q6=sQuery(id+"F15.wireOp",VERTEX,"E154");
            var Q7;
            Q7=sQuery(id+"F15.wireOp",VERTEX,"E155");
            var Q8;
            Q8=makeQuery(id+"F11.opPattern","COPY",BODY,{"derivedFrom":makeQuery(id+"F6.opExtrude","SWEPT_BODY",BODY,{"disambiguationData":[OSD([sQuery(id+"F5.wireOp",EDGE,"E15"),sQuery(id+"F5.wireOp",EDGE,"E16"),sQuery(id+"F5.wireOp",EDGE,"E17"),sQuery(id+"F5.wireOp",EDGE,"E18"),sQuery(id+"F5.wireOp",EDGE,"E19"),sQuery(id+"F5.wireOp",EDGE,"E20")])]}),"instanceName":"1"});
            hole(context, id + "F16", {"style" : HoleStyle.SIMPLE, "endStyle" : HoleEndStyle.BLIND, "holeDiameter" : 15.88 * mm, "majorDiameter" : 6.35 * mm, "holeDepth" : 6.35 * mm, "isTappedThrough" : true, "tappedDepth" : 22.25 * mm, "tapClearance" : 3, "locations" : qUnion([Q0, Q1, Q2, Q3, Q4, Q5, Q6, Q7]), "scope" : qUnion([Q8])});
        }
        {
            var Q0;
            Q0=qCreatedBy(makeId("Front.planeOp"),FACE);
            var sketch = newSketch(context, id + "F17", { "sketchPlane" : qUnion([Q0])});
            skLineSegment(sketch, "E162.bottom", {"start": v(-590.24, -50.8) * mm, "end": v(-945.84, -50.8) * mm});
            skLineSegment(sketch, "E162.top", {"start": v(-590.24, -254) * mm, "end": v(-945.84, -254) * mm});
            skLineSegment(sketch, "E162.left", {"start": v(-590.24, -50.8) * mm, "end": v(-590.24, -254) * mm});
            skLineSegment(sketch, "E162.right", {"start": v(-945.84, -50.8) * mm, "end": v(-945.84, -254) * mm});
            skLineSegment(sketch, "E163", {"start": v(-768.04, -50.8) * mm, "end": v(-768.04, -254) * mm, "construction": true});
            skLineSegment(sketch, "E164", {"start": v(-895.04, -50.8) * mm, "end": v(-895.04, -254) * mm, "construction": true});
            skLineSegment(sketch, "E165", {"start": v(-920.44, -50.8) * mm, "end": v(-920.44, -254) * mm, "construction": true});
            skLineSegment(sketch, "E166", {"start": v(-945.84, -152.4) * mm, "end": v(-590.24, -152.4) * mm, "construction": true});
            skLineSegment(sketch, "E167", {"start": v(-945.84, -63.5) * mm, "end": v(-768.04, -63.5) * mm, "construction": true});
            skPoint(sketch, "E168", {"position": v(-920.44, -63.5) * mm});
            skPoint(sketch, "E169", {"position": v(-895.04, -63.5) * mm});
            skPoint(sketch, "E170.MirrorP", {"position": v(-920.44, -241.3) * mm});
            skPoint(sketch, "E171.MirrorP", {"position": v(-895.04, -241.3) * mm});
            skPoint(sketch, "E172.MirrorP", {"position": v(-641.04, -241.3) * mm});
            skPoint(sketch, "E173.MirrorP", {"position": v(-615.64, -241.3) * mm});
            skPoint(sketch, "E174.MirrorP", {"position": v(-641.04, -63.5) * mm});
            skPoint(sketch, "E175.MirrorP", {"position": v(-615.64, -63.5) * mm});
            skSolve(sketch);
        }
        {
            var Q0;
            Q0 = qSketchRegion(id + "F17", true);
            extrude(context, id + "F18", {"entities" : qUnion([Q0]), "depth" : 6.35 * mm, "offsetDistance" : 25.4 * mm});
        }
        {
            var Q0;
            Q0=sQuery(id+"F17.wireOp",VERTEX,"E168");
            var Q1;
            Q1=sQuery(id+"F17.wireOp",VERTEX,"E169");
            var Q2;
            Q2=sQuery(id+"F17.wireOp",VERTEX,"E174.MirrorP");
            var Q3;
            Q3=sQuery(id+"F17.wireOp",VERTEX,"E175.MirrorP");
            var Q4;
            Q4=sQuery(id+"F17.wireOp",VERTEX,"E173.MirrorP");
            var Q5;
            Q5=sQuery(id+"F17.wireOp",VERTEX,"E172.MirrorP");
            var Q6;
            Q6=sQuery(id+"F17.wireOp",VERTEX,"E170.MirrorP");
            var Q7;
            Q7=sQuery(id+"F17.wireOp",VERTEX,"E171.MirrorP");
            var Q8;
            Q8=makeQuery(id+"F18.opExtrude","SWEPT_BODY",BODY,{"disambiguationData":[OSD([sQuery(id+"F17.wireOp",EDGE,"E162.bottom"),sQuery(id+"F17.wireOp",EDGE,"E162.top"),sQuery(id+"F17.wireOp",EDGE,"E162.left"),sQuery(id+"F17.wireOp",EDGE,"E162.right")])]});
            hole(context, id + "F19", {"style" : HoleStyle.SIMPLE, "endStyle" : HoleEndStyle.BLIND, "oppositeDirection" : true, "standardTappedOrClearance" : lookupTablePath({ "fit" : "Normal (ASME)", "standard" : "ANSI", "size" : "1/4", "type" : "Clearance" }), "standardBlindInLast" : lookupTablePath({ "fit" : "Normal", "standard" : "ANSI", "engagement" : "75%", "pitch" : "20 tpi", "size" : "1/4", "type" : "Clearance & tapped" }), "holeDiameter" : 7.14 * mm, "majorDiameter" : 6.35 * mm, "holeDepth" : 26.06 * mm, "isTappedThrough" : true, "tappedDepth" : 22.25 * mm, "tapClearance" : 3, "locations" : qUnion([Q0, Q1, Q2, Q3, Q4, Q5, Q6, Q7]), "scope" : qUnion([Q8])});
        }
        {
            var Q0;
            Q0=makeQuery(id+"F18.opExtrude","CAP_FACE",FACE,{"disambiguationData":[OSD([sQuery(id+"F17.wireOp",EDGE,"E162.bottom"),sQuery(id+"F17.wireOp",EDGE,"E162.top"),sQuery(id+"F17.wireOp",EDGE,"E162.left"),sQuery(id+"F17.wireOp",EDGE,"E162.right")])],"isStart":false});
            var sketch = newSketch(context, id + "F20", { "sketchPlane" : qUnion([Q0])});
            skLineSegment(sketch, "E176", {"start": v(-768.04, -50.8) * mm, "end": v(-768.04, -254) * mm, "construction": true});
            skLineSegment(sketch, "E177", {"start": v(-945.84, -152.4) * mm, "end": v(-590.24, -152.4) * mm, "construction": true});
            skPoint(sketch, "E178", {"position": v(-768.04, -152.4) * mm});
            skPoint(sketch, "E179", {"position": v(-793.59, -181.13) * mm});
            skPoint(sketch, "E180", {"position": v(-775.76, -190.04) * mm});
            skPoint(sketch, "E181", {"position": v(-755.87, -189.13) * mm});
            skPoint(sketch, "E182", {"position": v(-739.66, -196.11) * mm});
            skLineSegment(sketch, "E183", {"start": v(-945.84, -101.6) * mm, "end": v(-590.24, -101.6) * mm, "construction": true});
            skPoint(sketch, "E184", {"position": v(-893.9, -101.6) * mm});
            skPoint(sketch, "E185", {"position": v(-632.65, -101.6) * mm});
            skSolve(sketch);
        }
        {
            var Q0;
            Q0=sQuery(id+"F20.wireOp",VERTEX,"E179");
            var Q1;
            Q1=sQuery(id+"F20.wireOp",VERTEX,"E180");
            var Q2;
            Q2=sQuery(id+"F20.wireOp",VERTEX,"E181");
            var Q3;
            Q3=sQuery(id+"F20.wireOp",VERTEX,"E182");
            var Q4;
            Q4=sQuery(id+"F20.wireOp",VERTEX,"E185");
            var Q5;
            Q5=makeQuery(id+"F18.opExtrude","SWEPT_BODY",BODY,{"disambiguationData":[OSD([sQuery(id+"F17.wireOp",EDGE,"E162.bottom"),sQuery(id+"F17.wireOp",EDGE,"E162.top"),sQuery(id+"F17.wireOp",EDGE,"E162.left"),sQuery(id+"F17.wireOp",EDGE,"E162.right")])]});
            hole(context, id + "F21", {"style" : HoleStyle.SIMPLE, "endStyle" : HoleEndStyle.BLIND, "standardTappedOrClearance" : lookupTablePath({ "fit" : "Close (ASME)", "standard" : "ANSI", "size" : "1/4", "type" : "Clearance" }), "standardBlindInLast" : lookupTablePath({ "fit" : "Close", "standard" : "ANSI", "engagement" : "75%", "pitch" : "20 tpi", "size" : "1/4", "type" : "Clearance & tapped" }), "holeDiameter" : 6.76 * mm, "majorDiameter" : 6.35 * mm, "holeDepth" : 26.06 * mm, "isTappedThrough" : true, "tappedDepth" : 22.25 * mm, "tapClearance" : 3, "locations" : qUnion([Q0, Q1, Q2, Q3, Q4]), "scope" : qUnion([Q5])});
        }
        {
            var Q0;
            Q0=sQuery(id+"F20.wireOp",VERTEX,"E178");
            var Q1;
            Q1=sQuery(id+"F20.wireOp",VERTEX,"E184");
            var Q2;
            Q2=makeQuery(id+"F18.opExtrude","SWEPT_BODY",BODY,{"disambiguationData":[OSD([sQuery(id+"F17.wireOp",EDGE,"E162.bottom"),sQuery(id+"F17.wireOp",EDGE,"E162.top"),sQuery(id+"F17.wireOp",EDGE,"E162.left"),sQuery(id+"F17.wireOp",EDGE,"E162.right")])]});
            hole(context, id + "F22", {"style" : HoleStyle.SIMPLE, "endStyle" : HoleEndStyle.THROUGH, "holeDiameter" : 15.62 * mm, "majorDiameter" : 6.35 * mm, "isTappedThrough" : true, "tappedDepth" : 22.25 * mm, "tapClearance" : 3, "locations" : qUnion([Q0, Q1]), "scope" : qUnion([Q2])});
        }
        {
            var Q0;
            Q0=makeQuery(id+"F18.opExtrude","SWEPT_BODY",BODY,{"disambiguationData":[OSD([sQuery(id+"F17.wireOp",EDGE,"E162.bottom"),sQuery(id+"F17.wireOp",EDGE,"E162.top"),sQuery(id+"F17.wireOp",EDGE,"E162.left"),sQuery(id+"F17.wireOp",EDGE,"E162.right")])]});
            var Q1;
            Q1=makeQuery(id+"F18.opExtrude","CAP_FACE",FACE,{"disambiguationData":[OSD([sQuery(id+"F17.wireOp",EDGE,"E162.bottom"),sQuery(id+"F17.wireOp",EDGE,"E162.top"),sQuery(id+"F17.wireOp",EDGE,"E162.left"),sQuery(id+"F17.wireOp",EDGE,"E162.right")])],"isStart":false});
            transform(context, id + "F23", {"entities" : qUnion([Q0]), "transformType" : TransformType.TRANSLATION_DISTANCE, "transformDirection" : qUnion([Q1]), "distance" : 355.6 * mm, "makeCopy" : true});
        }
        {
            var Q0;
            Q0=makeQuery(id+"F23.opPattern","COPY",FACE,{"derivedFrom":makeQuery(id+"F18.opExtrude","CAP_FACE",FACE,{"disambiguationData":[OSD([sQuery(id+"F17.wireOp",EDGE,"E162.bottom"),sQuery(id+"F17.wireOp",EDGE,"E162.top"),sQuery(id+"F17.wireOp",EDGE,"E162.left"),sQuery(id+"F17.wireOp",EDGE,"E162.right")])],"isStart":false}),"instanceName":"1"});
            var sketch = newSketch(context, id + "F24", { "sketchPlane" : qUnion([Q0])});
            skLineSegment(sketch, "E186", {"start": v(-945.84, -152.4) * mm, "end": v(-590.24, -152.4) * mm, "construction": true});
            skLineSegment(sketch, "E187", {"start": v(-768.04, -50.8) * mm, "end": v(-768.04, -254) * mm, "construction": true});
            skLineSegment(sketch, "E188", {"start": v(-641.04, -204.9) * mm, "end": v(-641.04, -151.22) * mm});
            skLineSegment(sketch, "E189", {"start": v(-742.64, -95.25) * mm, "end": v(-742.64, -153.58) * mm});
            skLineSegment(sketch, "E190", {"start": v(-739.46, -159.07) * mm, "end": v(-650.56, -210.4) * mm});
            skLineSegment(sketch, "E191.MirrorCS", {"start": v(-793.44, -95.25) * mm, "end": v(-793.44, -153.58) * mm});
            skLineSegment(sketch, "E192.MirrorCS", {"start": v(-796.61, -159.07) * mm, "end": v(-885.51, -210.4) * mm});
            skLineSegment(sketch, "E193.MirrorCS", {"start": v(-895.04, -204.9) * mm, "end": v(-895.04, -151.22) * mm});
            skLineSegment(sketch, "E194", {"start": v(-857.95, -253.15) * mm, "end": v(-771.21, -203.07) * mm});
            skLineSegment(sketch, "E195", {"start": v(-764.86, -203.07) * mm, "end": v(-678.12, -253.15) * mm});
            skPoint(sketch, "E196.visualSharp", {"position": v(-895.04, -215.9) * mm});
            skArc(sketch, "E196.filletArc", {"start": v(-895.04, -204.9) * mm, "mid": v(-891.86, -210.4) * mm, "end": v(-885.51, -210.4) * mm});
            skPoint(sketch, "E197.visualSharp", {"position": v(-793.44, -157.24) * mm});
            skArc(sketch, "E197.filletArc", {"start": v(-796.61, -159.07) * mm, "mid": v(-794.29, -156.75) * mm, "end": v(-793.44, -153.58) * mm});
            skPoint(sketch, "E198.visualSharp", {"position": v(-895.04, -147.56) * mm});
            skArc(sketch, "E198.filletArc", {"start": v(-891.86, -145.73) * mm, "mid": v(-894.18, -148.05) * mm, "end": v(-895.04, -151.22) * mm});
            skPoint(sketch, "E199.visualSharp", {"position": v(-793.44, -88.9) * mm});
            skArc(sketch, "E199.filletArc", {"start": v(-793.44, -95.25) * mm, "mid": v(-795.3, -90.76) * mm, "end": v(-799.79, -88.9) * mm});
            skPoint(sketch, "E200.visualSharp", {"position": v(-742.64, -88.9) * mm});
            skPoint(sketch, "E201.visualSharp", {"position": v(-742.64, -157.24) * mm});
            skArc(sketch, "E201.filletArc", {"start": v(-742.64, -153.58) * mm, "mid": v(-741.78, -156.75) * mm, "end": v(-739.46, -159.07) * mm});
            skPoint(sketch, "E202.visualSharp", {"position": v(-641.04, -147.56) * mm});
            skArc(sketch, "E202.filletArc", {"start": v(-641.04, -151.22) * mm, "mid": v(-641.89, -148.05) * mm, "end": v(-644.21, -145.73) * mm});
            skPoint(sketch, "E203.visualSharp", {"position": v(-641.04, -215.9) * mm});
            skArc(sketch, "E203.filletArc", {"start": v(-650.56, -210.4) * mm, "mid": v(-644.21, -210.4) * mm, "end": v(-641.04, -204.9) * mm});
            skPoint(sketch, "E204.visualSharp", {"position": v(-768.04, -201.24) * mm});
            skArc(sketch, "E204.filletArc", {"start": v(-764.86, -203.07) * mm, "mid": v(-768.04, -202.22) * mm, "end": v(-771.21, -203.07) * mm});
            skLineSegment(sketch, "E205", {"start": v(-945.84, -254) * mm, "end": v(-861.13, -254) * mm});
            skLineSegment(sketch, "E206", {"start": v(-674.94, -254) * mm, "end": v(-590.24, -254) * mm});
            skPoint(sketch, "E207.visualSharp", {"position": v(-859.43, -254) * mm});
            skArc(sketch, "E207.filletArc", {"start": v(-861.13, -254) * mm, "mid": v(-859.48, -253.78) * mm, "end": v(-857.95, -253.15) * mm});
            skPoint(sketch, "E208.visualSharp", {"position": v(-676.64, -254) * mm});
            skArc(sketch, "E208.filletArc", {"start": v(-678.12, -253.15) * mm, "mid": v(-676.59, -253.78) * mm, "end": v(-674.94, -254) * mm});
            skArc(sketch, "E209", {"start": v(-891.86, -145.73) * mm, "mid": v(-860.09, -130.04) * mm, "end": v(-850.07, -96.05) * mm});
            skLineSegment(sketch, "E210", {"start": v(-799.79, -88.9) * mm, "end": v(-843.77, -88.9) * mm});
            skPoint(sketch, "E211.visualSharp", {"position": v(-851.58, -88.9) * mm});
            skArc(sketch, "E211.filletArc", {"start": v(-843.77, -88.9) * mm, "mid": v(-848.53, -91.05) * mm, "end": v(-850.07, -96.05) * mm});
            skArc(sketch, "E212.MirrorCS", {"start": v(-644.21, -145.73) * mm, "mid": v(-675.98, -130.04) * mm, "end": v(-686, -96.05) * mm});
            skLineSegment(sketch, "E213.MirrorCS", {"start": v(-736.29, -88.9) * mm, "end": v(-692.3, -88.9) * mm});
            skArc(sketch, "E214.MirrorCS", {"start": v(-742.64, -95.25) * mm, "mid": v(-740.78, -90.76) * mm, "end": v(-736.29, -88.9) * mm});
            skArc(sketch, "E215.MirrorCS", {"start": v(-692.3, -88.9) * mm, "mid": v(-687.54, -91.05) * mm, "end": v(-686, -96.05) * mm});
            skSolve(sketch);
        }
        {
            var Q0;
            Q0 = qSketchRegion(id + "F24", true);
            var Q1;
            Q1=makeQuery(id+"F24.imprint","IMPRINT",FACE,{"disambiguationData":[TD([[makeQuery(id+"F24.imprint","IMPRINT",EDGE,{"derivedFrom":sQuery(id+"F24.wireOp",EDGE,"E194")}),-1.0]])]});
            extrude(context, id + "F25", {"entities" : qUnion([Q0, Q1]), "operationType" : NewBodyOperationType.REMOVE, "oppositeDirection" : true, "depth" : 6.35 * mm, "offsetDistance" : 25.4 * mm});
        }
        {
            var Q0;
            Q0=makeQuery(id+"F18.opExtrude","SWEPT_BODY",BODY,{"disambiguationData":[OSD([sQuery(id+"F17.wireOp",EDGE,"E162.bottom"),sQuery(id+"F17.wireOp",EDGE,"E162.top"),sQuery(id+"F17.wireOp",EDGE,"E162.left"),sQuery(id+"F17.wireOp",EDGE,"E162.right")])]});
            var Q1;
            Q1=makeQuery(id+"F1.opExtrude","SWEPT_FACE",FACE,{"disambiguationData":[OSD([sQuery(id+"F0.wireOp",EDGE,"E0.right")])]});
            mirror(context, id + "F26", {"entities" : qUnion([Q0]), "mirrorPlane" : qUnion([Q1])});
        }
        {
            var Q0;
            Q0=makeQuery(id+"F23.opPattern","COPY",BODY,{"derivedFrom":makeQuery(id+"F18.opExtrude","SWEPT_BODY",BODY,{"disambiguationData":[OSD([sQuery(id+"F17.wireOp",EDGE,"E162.bottom"),sQuery(id+"F17.wireOp",EDGE,"E162.top"),sQuery(id+"F17.wireOp",EDGE,"E162.left"),sQuery(id+"F17.wireOp",EDGE,"E162.right")])]}),"instanceName":"1"});
            var Q1;
            Q1=makeQuery(id+"F1.opExtrude","SWEPT_FACE",FACE,{"disambiguationData":[OSD([sQuery(id+"F0.wireOp",EDGE,"E0.right")])]});
            mirror(context, id + "F27", {"entities" : qUnion([Q0]), "mirrorPlane" : qUnion([Q1])});
        }
    });
